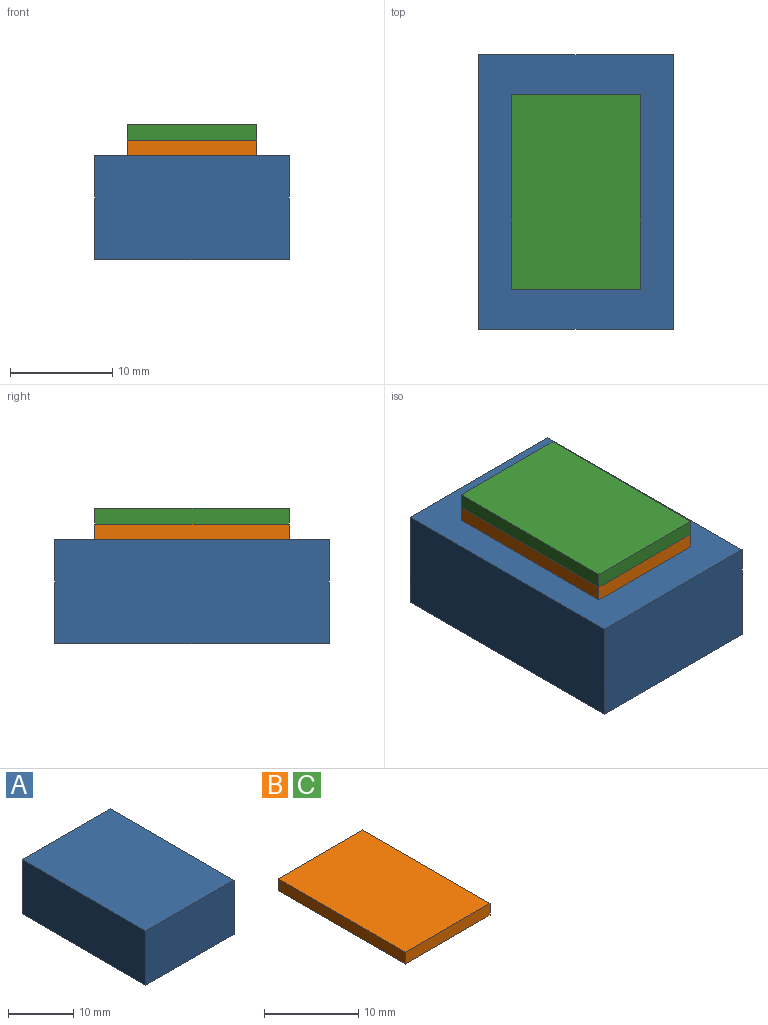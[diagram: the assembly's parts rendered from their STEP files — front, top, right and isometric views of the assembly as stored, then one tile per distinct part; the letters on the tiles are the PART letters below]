
ASSEMBLY  parts=3 mates=2
PART A: 6 faces, bbox 19.1x26.8x10.2 mm
  f0: plane 19.05x10.16mm, normal (0,-1,0), area 193.5mm2, adj f1,f3,f4,f5
  f1: plane 26.82x10.16mm, normal (1,0,0), area 272.5mm2, adj f0,f2,f4,f5
  f2: plane 19.05x10.16mm, normal (0,1,0), area 193.5mm2, adj f1,f3,f4,f5
  f3: plane 26.82x10.16mm, normal (-1,0,0), area 272.5mm2, adj f0,f2,f4,f5
  f4: plane 26.82x19.05mm, normal (0,0,1), area 511mm2, adj f0,f1,f2,f3
  f5: plane 26.82x19.05mm, normal (0,0,-1), area 511mm2, adj f0,f1,f2,f3
PART B: 6 faces, bbox 12.7x19.1x1.5 mm
  f0: plane 12.7x1.52mm, normal (0,-1,0), area 19.4mm2, adj f1,f3,f4,f5
  f1: plane 19.05x1.52mm, normal (1,0,0), area 29mm2, adj f0,f2,f4,f5
  f2: plane 12.7x1.52mm, normal (0,1,0), area 19.4mm2, adj f1,f3,f4,f5
  f3: plane 19.05x1.52mm, normal (-1,0,0), area 29mm2, adj f0,f2,f4,f5
  f4: plane 19.05x12.7mm, normal (0,0,1), area 241.9mm2, adj f0,f1,f2,f3
  f5: plane 19.05x12.7mm, normal (0,0,-1), area 241.9mm2, adj f0,f1,f2,f3
PART C: same geometry as B
PLACE A t=(-260.17,11.5,17.77)mm
PLACE B t=(-260.17,11.5,27.93)mm
PLACE C t=(-260.17,11.5,29.45)mm
MATE fastened B.f4 <-> C.f5  axis (0,0,1) through (-260.17,11.5,29.45)mm
MATE fastened B.f5 <-> A.f4  axis (0,0,-1) through (-260.17,11.5,27.93)mm
